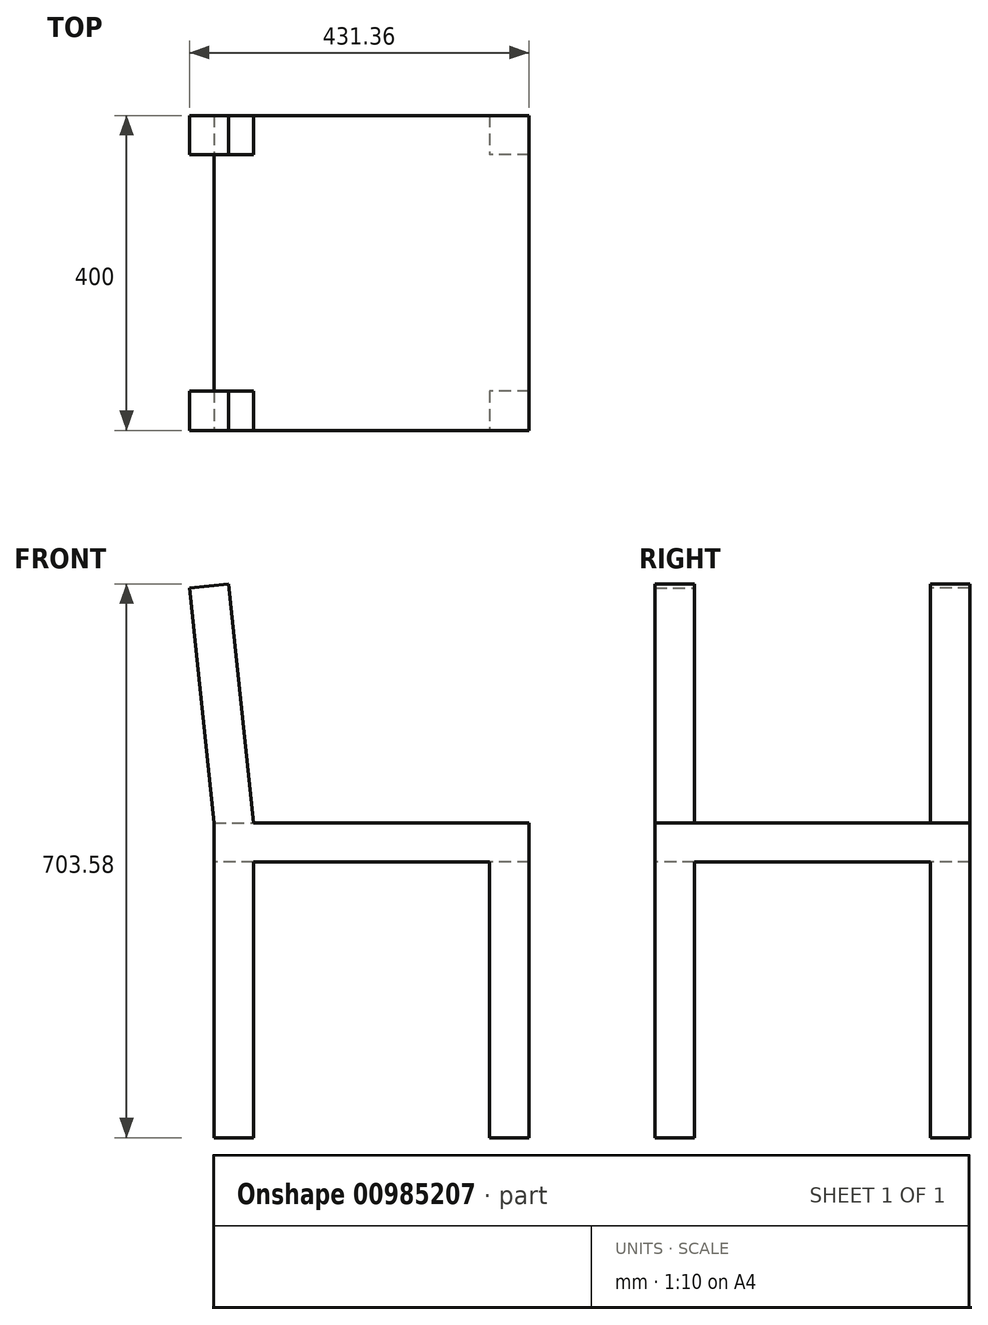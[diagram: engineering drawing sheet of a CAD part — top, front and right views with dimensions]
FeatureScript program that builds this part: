
annotation { "Feature Type Name" : "Feature", "Feature Type Description" : "" }
export const myFeature = defineFeature(function(context is Context, id is Id, definition is map)
    precondition{}
    {
        {
            var Q0;
            Q0=qCreatedBy(makeId("Top.planeOp"),FACE);
            var sketch = newSketch(context, id + "F0", { "sketchPlane" : qUnion([Q0])});
            skLineSegment(sketch, "E0.bottom", {"start": v(-200.36, 246.71) * mm, "end": v(199.64, 246.71) * mm});
            skLineSegment(sketch, "E0.top", {"start": v(-200.36, -153.29) * mm, "end": v(199.64, -153.29) * mm});
            skLineSegment(sketch, "E0.left", {"start": v(-200.36, 246.71) * mm, "end": v(-200.36, -153.29) * mm});
            skLineSegment(sketch, "E0.right", {"start": v(199.64, 246.71) * mm, "end": v(199.64, -153.29) * mm});
            skSolve(sketch);
        }
        {
            var Q0;
            Q0=makeQuery(id+"F0.imprint","IMPRINT",FACE,{"disambiguationData":[TD([[makeQuery(id+"F0.imprint","IMPRINT",EDGE,{"derivedFrom":sQuery(id+"F0.wireOp",EDGE,"E0.bottom")}),-1.0]])]});
            extrude(context, id + "F1", {"entities" : qUnion([Q0]), "depth" : 400 * mm, "offsetDistance" : 25 * mm});
        }
        {
            var Q0;
            Q0=makeQuery(id+"F1.opExtrude","SWEPT_FACE",FACE,{"disambiguationData":[OSD([sQuery(id+"F0.wireOp",EDGE,"E0.left")])]});
            var sketch = newSketch(context, id + "F2", { "sketchPlane" : qUnion([Q0])});
            skLineSegment(sketch, "E1", {"start": v(-196.71, 0) * mm, "end": v(-196.71, 350) * mm});
            skLineSegment(sketch, "E2", {"start": v(-196.71, 350) * mm, "end": v(103.29, 350) * mm});
            skLineSegment(sketch, "E3", {"start": v(103.29, 350) * mm, "end": v(103.29, 0) * mm});
            skSolve(sketch);
        }
        {
            var Q0;
            {var subQ0=sQuery(id+"F2.wireOp",EDGE,"E1");Q0=makeQuery(id+"F2.imprint","IMPRINT",FACE,{"disambiguationData":[TD([[makeQuery(id+"F2.imprint","IMPRINT",EDGE,{"derivedFrom":subQ0}),-1.0]])]});}
            extrude(context, id + "F3", {"entities" : qUnion([Q0]), "operationType" : NewBodyOperationType.REMOVE, "oppositeDirection" : true, "depth" : 400 * mm, "offsetDistance" : 25 * mm});
        }
        {
            var Q0;
            Q0=makeQuery(id+"F1.opExtrude","SWEPT_FACE",FACE,{"disambiguationData":[OSD([sQuery(id+"F0.wireOp",EDGE,"E0.top")])]});
            var sketch = newSketch(context, id + "F4", { "sketchPlane" : qUnion([Q0])});
            skLineSegment(sketch, "E4", {"start": v(-150.36, 0) * mm, "end": v(-150.36, 350) * mm});
            skLineSegment(sketch, "E5", {"start": v(-150.36, 350) * mm, "end": v(149.64, 350) * mm});
            skLineSegment(sketch, "E6", {"start": v(149.64, 350) * mm, "end": v(149.64, 0) * mm});
            skSolve(sketch);
        }
        {
            var Q0;
            {var subQ0=sQuery(id+"F4.wireOp",EDGE,"E4");Q0=makeQuery(id+"F4.imprint","IMPRINT",FACE,{"disambiguationData":[TD([[makeQuery(id+"F4.imprint","IMPRINT",EDGE,{"derivedFrom":subQ0}),-1.0]])]});}
            extrude(context, id + "F5", {"entities" : qUnion([Q0]), "operationType" : NewBodyOperationType.REMOVE, "oppositeDirection" : true, "depth" : 400 * mm, "offsetDistance" : 25 * mm});
        }
        {
            var Q0;
            Q0=makeQuery(id+"F1.opExtrude","CAP_FACE",FACE,{"disambiguationData":[OSD([sQuery(id+"F0.wireOp",EDGE,"E0.bottom"),sQuery(id+"F0.wireOp",EDGE,"E0.top"),sQuery(id+"F0.wireOp",EDGE,"E0.left"),sQuery(id+"F0.wireOp",EDGE,"E0.right")])],"isStart":false});
            var sketch = newSketch(context, id + "F6", { "sketchPlane" : qUnion([Q0])});
            skLineSegment(sketch, "E7", {"start": v(-150.36, 246.71) * mm, "end": v(-150.36, -153.29) * mm});
            skSolve(sketch);
        }
        {
            var Q0;
            {var subQ0=sQuery(id+"F6.wireOp",EDGE,"E7");Q0=makeQuery(id+"F6.imprint","IMPRINT",FACE,{"disambiguationData":[TD([[makeQuery(id+"F6.imprint","IMPRINT",EDGE,{"derivedFrom":subQ0}),-1.0]])]});}
            extrude(context, id + "F7", {"entities" : qUnion([Q0]), "operationType" : NewBodyOperationType.ADD, "depth" : 300 * mm, "offsetDistance" : 25 * mm});
        }
        {
            var Q0;
            Q0=makeQuery(id+"F7.opExtrude","SWEPT_FACE",FACE,{"disambiguationData":[OSD([sQuery(id+"F6.wireOp",EDGE,"E7")])]});
            var sketch = newSketch(context, id + "F8", { "sketchPlane" : qUnion([Q0])});
            skLineSegment(sketch, "E8", {"start": v(-103.29, 400) * mm, "end": v(-103.29, 700) * mm});
            skLineSegment(sketch, "E9", {"start": v(196.71, 400) * mm, "end": v(196.71, 700) * mm});
            skSolve(sketch);
        }
        {
            var Q0;
            {var subQ0=sQuery(id+"F8.wireOp",EDGE,"E8");Q0=makeQuery(id+"F8.imprint","IMPRINT",FACE,{"disambiguationData":[TD([[makeQuery(id+"F8.imprint","IMPRINT",EDGE,{"derivedFrom":subQ0}),-1.0]])]});}
            extrude(context, id + "F9", {"entities" : qUnion([Q0]), "operationType" : NewBodyOperationType.REMOVE, "oppositeDirection" : true, "depth" : 50 * mm, "offsetDistance" : 25 * mm});
        }
        {
            var Q0;
            {var subQ0=sQuery(id+"F6.wireOp",EDGE,"E7");var subQ1=sQuery(id+"F0.wireOp",EDGE,"E0.left");var subQ2=sQuery(id+"F0.wireOp",EDGE,"E0.top");Q0=makeQuery(id+"F9.boolean.opBoolean","SPLIT",FACE,{"disambiguationData":[TD([makeQuery(id+"F1.opExtrude","SWEPT_FACE",FACE,{"disambiguationData":[OSD([subQ2])]})])],"derivedFrom":makeQuery(id+"F7.opExtrude","CAP_FACE",FACE,{"disambiguationData":[OSD([sQuery(id+"F0.wireOp",EDGE,"E0.bottom"),subQ2,subQ1,subQ0])],"isStart":false})});}
            extrude(context, id + "F10", {"entities" : qUnion([Q0]), "operationType" : NewBodyOperationType.REMOVE, "oppositeDirection" : true, "depth" : 300 * mm, "offsetDistance" : 25 * mm});
        }
        {
            var Q0;
            {var subQ0=sQuery(id+"F6.wireOp",EDGE,"E7");var subQ1=sQuery(id+"F0.wireOp",EDGE,"E0.bottom");var subQ2=sQuery(id+"F0.wireOp",EDGE,"E0.left");Q0=makeQuery(id+"F9.boolean.opBoolean","SPLIT",FACE,{"disambiguationData":[TD([makeQuery(id+"F1.opExtrude","SWEPT_FACE",FACE,{"disambiguationData":[OSD([subQ1])]})])],"derivedFrom":makeQuery(id+"F7.opExtrude","CAP_FACE",FACE,{"disambiguationData":[OSD([subQ1,sQuery(id+"F0.wireOp",EDGE,"E0.top"),subQ2,subQ0])],"isStart":false})});}
            extrude(context, id + "F11", {"entities" : qUnion([Q0]), "operationType" : NewBodyOperationType.REMOVE, "oppositeDirection" : true, "depth" : 300 * mm, "offsetDistance" : 25 * mm});
        }
        {
            var Q0;
            {var subQ0=sQuery(id+"F6.wireOp",EDGE,"E7");var subQ1=sQuery(id+"F0.wireOp",EDGE,"E0.left");var subQ2=sQuery(id+"F0.wireOp",EDGE,"E0.top");var subQ3=sQuery(id+"F0.wireOp",EDGE,"E0.bottom");var subQ4=makeQuery(id+"F7.opExtrude","CAP_EDGE",EDGE,{"disambiguationData":[OSD([subQ0])],"isStart":true});Q0=makeQuery(id+"F11.boolean.opBoolean","MERGE",FACE,{"derivedFrom":[makeQuery(id+"F10.boolean.opBoolean","MERGE",FACE,{"derivedFrom":[makeQuery(id+"F9.boolean.opBoolean","MERGE",FACE,{"derivedFrom":[makeQuery(id+"F1.opExtrude","CAP_FACE",FACE,{"disambiguationData":[OSD([subQ3,subQ2,subQ1,sQuery(id+"F0.wireOp",EDGE,"E0.right")])],"isStart":false})],"fromTools":[makeQuery(id+"F9.opExtrude","SWEPT_FACE",FACE,{"disambiguationData":[OSD([subQ0]),TDD([makeQuery(id+"F8.imprint","IMPRINT",EDGE,{"disambiguationData":[TD([[makeQuery(id+"F8.imprint","INTERSECT",VERTEX,{"derivedFrom":[subQ4,sQuery(id+"F8.wireOp",EDGE,"E8")]}),1.0]])],"derivedFrom":subQ4})])]})]})],"fromTools":[makeQuery(id+"F10.opExtrude","CAP_FACE",FACE,{"disambiguationData":[OSD([subQ3,subQ2,subQ1,subQ0])],"isStart":false})]})],"fromTools":[makeQuery(id+"F11.opExtrude","CAP_FACE",FACE,{"disambiguationData":[OSD([subQ3,subQ2,subQ1,subQ0])],"isStart":false})]});}
            var sketch = newSketch(context, id + "F12", { "sketchPlane" : qUnion([Q0])});
            skLineSegment(sketch, "E10", {"start": v(-200.36, 309.28) * mm, "end": v(-200.36, -250.77) * mm, "construction": true});
            skSolve(sketch);
        }
        {
            var Q0;
            {var subQ0=sQuery(id+"F0.wireOp",EDGE,"E0.left");Q0=makeQuery(id+"F7.boolean.opBoolean","MERGE",FACE,{"derivedFrom":[makeQuery(id+"F1.opExtrude","SWEPT_FACE",FACE,{"disambiguationData":[OSD([subQ0])]}),makeQuery(id+"F7.opExtrude","SWEPT_FACE",FACE,{"disambiguationData":[OSD([subQ0])]})]});}
            cPlane(context, id + "F13", {"entities" : qUnion([Q0]), "cplaneType" : CPlaneType.OFFSET, "offset" : 0 * mm, "width" : 150 * mm, "height" : 150 * mm});
        }
        {
            var Q0;
            Q0=qCreatedBy(id+"F13.planeOp",FACE);
            var Q1;
            Q1=sQuery(id+"F12.wireOp",EDGE,"E10");
            cPlane(context, id + "F14", {"entities" : qUnion([Q0, Q1]), "cplaneType" : CPlaneType.LINE_ANGLE, "offset" : 25 * mm, "angle" : 6 * degree, "width" : 150 * mm, "height" : 150 * mm});
        }
        {
            var Q0;
            Q0=qCreatedBy(id+"F14.planeOp",FACE);
            var sketch = newSketch(context, id + "F15", { "sketchPlane" : qUnion([Q0])});
            skLineSegment(sketch, "E11.bottom", {"start": v(-153.29, 718.75) * mm, "end": v(-103.29, 718.75) * mm});
            skLineSegment(sketch, "E11.top", {"start": v(-153.29, 418.75) * mm, "end": v(-103.29, 418.75) * mm});
            skLineSegment(sketch, "E11.left", {"start": v(-153.29, 718.75) * mm, "end": v(-153.29, 418.75) * mm});
            skLineSegment(sketch, "E11.right", {"start": v(-103.29, 718.75) * mm, "end": v(-103.29, 418.75) * mm});
            skSolve(sketch);
        }
        {
            var Q0;
            Q0=makeQuery(id+"F15.imprint","IMPRINT",FACE,{"disambiguationData":[TD([[makeQuery(id+"F15.imprint","IMPRINT",EDGE,{"derivedFrom":sQuery(id+"F15.wireOp",EDGE,"E11.bottom")}),-1.0]])]});
            extrude(context, id + "F16", {"entities" : qUnion([Q0]), "operationType" : NewBodyOperationType.ADD, "depth" : 50 * mm, "offsetDistance" : 25 * mm});
        }
        {
            var Q0;
            Q0=makeQuery(id+"F16.opExtrude","SWEPT_FACE",FACE,{"disambiguationData":[OSD([sQuery(id+"F15.wireOp",EDGE,"E11.top")])]});
            extrude(context, id + "F17", {"entities" : qUnion([Q0]), "operationType" : NewBodyOperationType.ADD, "depth" : 25 * mm, "offsetDistance" : 25 * mm});
        }
        {
            var Q0;
            Q0=qCreatedBy(id+"F14.planeOp",FACE);
            var sketch = newSketch(context, id + "F18", { "sketchPlane" : qUnion([Q0])});
            skLineSegment(sketch, "E12.bottom", {"start": v(246.71, 718.75) * mm, "end": v(196.71, 718.75) * mm});
            skLineSegment(sketch, "E12.top", {"start": v(246.71, 418.75) * mm, "end": v(196.71, 418.75) * mm});
            skLineSegment(sketch, "E12.left", {"start": v(246.71, 718.75) * mm, "end": v(246.71, 418.75) * mm});
            skLineSegment(sketch, "E12.right", {"start": v(196.71, 718.75) * mm, "end": v(196.71, 418.75) * mm});
            skSolve(sketch);
        }
        {
            var Q0;
            Q0=makeQuery(id+"F18.imprint","IMPRINT",FACE,{"disambiguationData":[TD([[makeQuery(id+"F18.imprint","IMPRINT",EDGE,{"derivedFrom":sQuery(id+"F18.wireOp",EDGE,"E12.bottom")}),1.0]])]});
            extrude(context, id + "F19", {"entities" : qUnion([Q0]), "depth" : 50 * mm, "offsetDistance" : 25 * mm});
        }
        {
            var Q0;
            Q0=makeQuery(id+"F19.opExtrude","SWEPT_FACE",FACE,{"disambiguationData":[OSD([sQuery(id+"F18.wireOp",EDGE,"E12.top")])]});
            extrude(context, id + "F20", {"entities" : qUnion([Q0]), "operationType" : NewBodyOperationType.ADD, "endBound" : BoundingType.UP_TO_NEXT, "depth" : 25 * mm, "offsetDistance" : 25 * mm});
        }
    });
